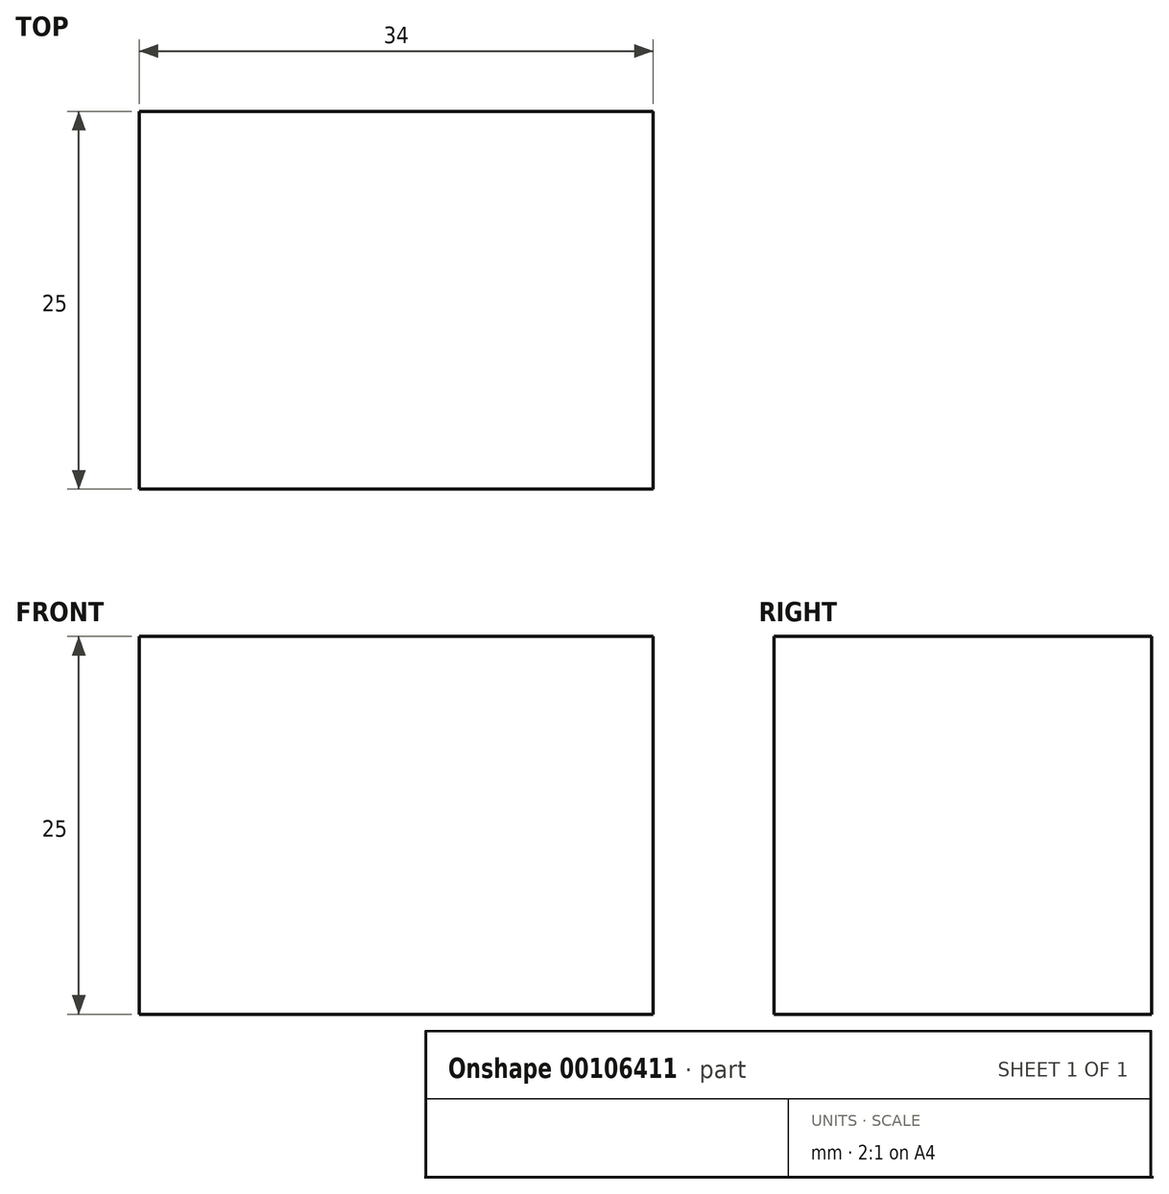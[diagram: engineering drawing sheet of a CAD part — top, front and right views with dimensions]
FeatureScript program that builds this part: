
annotation { "Feature Type Name" : "Feature", "Feature Type Description" : "" }
export const myFeature = defineFeature(function(context is Context, id is Id, definition is map)
    precondition{}
    {
        {
            var Q0;
            Q0=qCreatedBy(makeId("Right.planeOp"),FACE);
            var sketch = newSketch(context, id + "F0", { "sketchPlane" : qUnion([Q0])});
            skLineSegment(sketch, "E0.bottom", {"start": v(12.5, -12.5) * mm, "end": v(-12.5, -12.5) * mm});
            skLineSegment(sketch, "E0.top", {"start": v(12.5, 12.5) * mm, "end": v(-12.5, 12.5) * mm});
            skLineSegment(sketch, "E0.left", {"start": v(12.5, -12.5) * mm, "end": v(12.5, 12.5) * mm});
            skLineSegment(sketch, "E0.right", {"start": v(-12.5, -12.5) * mm, "end": v(-12.5, 12.5) * mm});
            skPoint(sketch, "E0.middle", {"position": v(0, 0) * mm});
            skSolve(sketch);
        }
        {
            var Q0;
            Q0=makeQuery(id+"F0.imprint","IMPRINT",FACE,{"disambiguationData":[TD([[makeQuery(id+"F0.imprint","IMPRINT",EDGE,{"derivedFrom":sQuery(id+"F0.wireOp",EDGE,"E0.bottom")}),-1.0]])]});
            extrude(context, id + "F1", {"entities" : qUnion([Q0]), "depth" : 34 * mm, "symmetric" : true});
        }
    });
